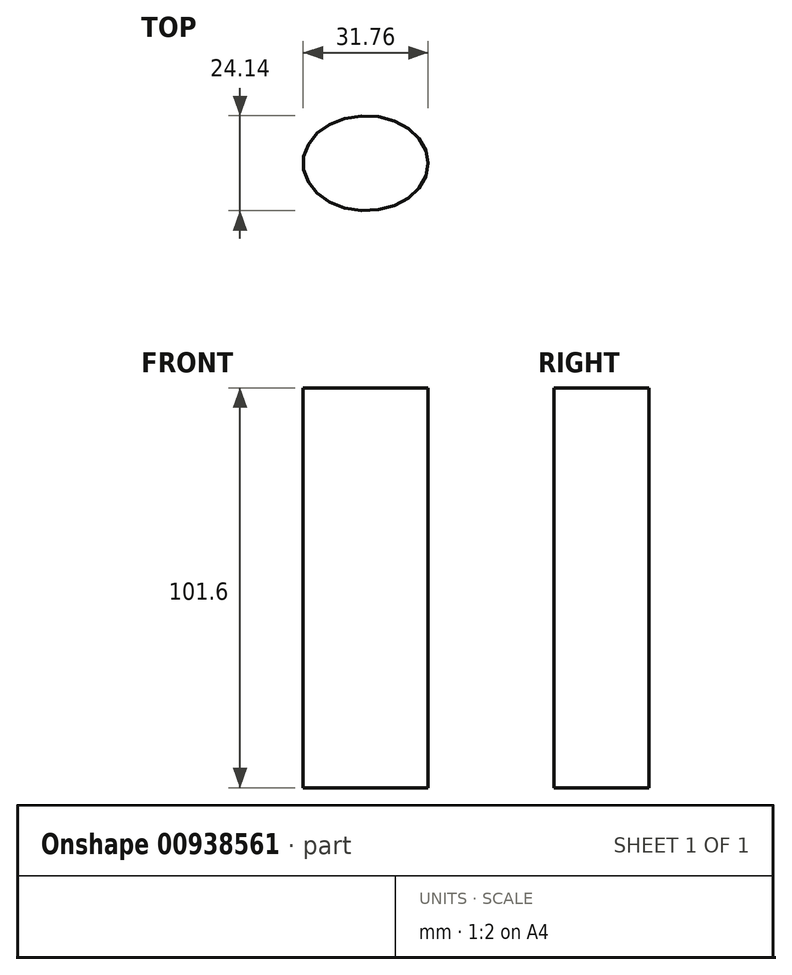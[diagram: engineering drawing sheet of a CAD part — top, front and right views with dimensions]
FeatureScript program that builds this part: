
annotation { "Feature Type Name" : "Feature", "Feature Type Description" : "" }
export const myFeature = defineFeature(function(context is Context, id is Id, definition is map)
    precondition{}
    {
        {
            var Q0;
            Q0=qCreatedBy(makeId("Top.planeOp"),FACE);
            var sketch = newSketch(context, id + "F0", { "sketchPlane" : qUnion([Q0])});
            skEllipse(sketch, "E0", {"center": v(0, 0) * mm, "majorRadius": 15.88 * mm, "minorRadius": 12.07 * mm, "majorAxis": v(1, 0)});
            skSolve(sketch);
        }
        {
            var Q0;
            Q0 = qSketchRegion(id + "F0", true);
            extrude(context, id + "F1", {"entities" : qUnion([Q0]), "depth" : 101.6 * mm, "offsetDistance" : 25.4 * mm});
        }
    });
